# Revit family: QF_BOURGEAT_Desinsectiseur_électrique
name_source: partatom
category: Equipement spécialisé
revit_build: Autodesk Revit 2015 (Build: 20140606_1530(x64)
units: mm (PartAtom-declared; Revit-internal decimal feet)

## types (3) — shared parameters
Fabricant = BOURGEAT
Fréquence = 50 Hz
Hauteur hors tout = 260 mm  [stored 0.853018 ft]
Indice de protection = 21
Intensité nominale = 0 A
Phase = 2
Profondeur hors tout = 140 mm  [stored 0.459318 ft]
Spécification du Fabricant = Desinsectiseur modèle électrique
Tension = 230 V
URL catalogue = http://www.bourgeat.fr

## per-type parameters (varying)
| type | Cote grille | Longueur hors tout | Modèle | Poids net à vide | Puissance électrique  | Tube actinique | nombre grille |
| Pour 40 m² | 24 mm | 360 mm  [stored 1.1811 ft] | 731109 | 4.00 kg | 25 W | 2 x 8 W | 6 |
| Pour 80 m² | 5 mm  [stored 0.0164042 ft] | 530 mm  [stored 1.73885 ft] | 731110 | 4.50 kg | 45 W | 2 x 15 W | 10 |
| Pour 240 m² | 18 mm  [stored 0.0590551 ft] | 660 mm  [stored 2.16535 ft] | 731111 | 8.50 kg | 105 W | 2 x 40 W | 12 |

note: [stored X ft] marks values corroborated as IEEE doubles in the binary element streams (Revit-internal decimal feet)
